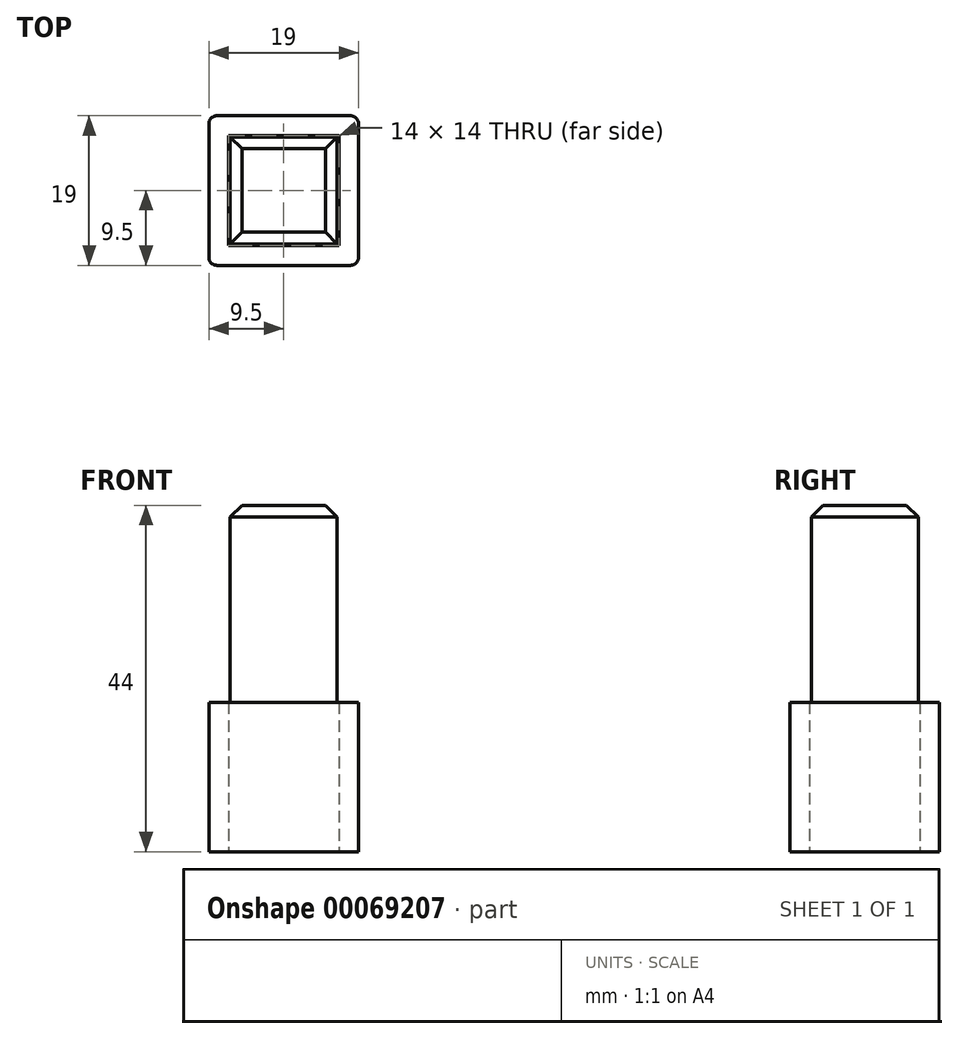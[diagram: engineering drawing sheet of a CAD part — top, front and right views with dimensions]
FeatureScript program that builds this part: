
annotation { "Feature Type Name" : "Feature", "Feature Type Description" : "" }
export const myFeature = defineFeature(function(context is Context, id is Id, definition is map)
    precondition{}
    {
        {
            var Q0;
            Q0=qCreatedBy(makeId("Top.planeOp"),FACE);
            var sketch = newSketch(context, id + "F0", { "sketchPlane" : qUnion([Q0])});
            skLineSegment(sketch, "E0.rect.bottom", {"start": v(9.5, 9.5) * mm, "end": v(-9.5, 9.5) * mm});
            skLineSegment(sketch, "E0.rect.top", {"start": v(9.5, -9.5) * mm, "end": v(-9.5, -9.5) * mm});
            skLineSegment(sketch, "E0.rect.left", {"start": v(9.5, 9.5) * mm, "end": v(9.5, -9.5) * mm});
            skLineSegment(sketch, "E0.rect.right", {"start": v(-9.5, 9.5) * mm, "end": v(-9.5, -9.5) * mm});
            skPoint(sketch, "E0.rect.middle", {"position": v(0, 0) * mm});
            skSolve(sketch);
        }
        {
            var Q0;
            Q0 = qSketchRegion(id + "F0", true);
            extrude(context, id + "F1", {"entities" : qUnion([Q0]), "depth" : (14 + 5) * mm});
        }
        {
            var Q0;
            Q0=makeQuery(id+"F1.opExtrude","CAP_FACE",FACE,{"disambiguationData":[OSD([sQuery(id+"F0.wireOp",EDGE,"E0.rect.bottom"),sQuery(id+"F0.wireOp",EDGE,"E0.rect.top"),sQuery(id+"F0.wireOp",EDGE,"E0.rect.left"),sQuery(id+"F0.wireOp",EDGE,"E0.rect.right")])],"isStart":false});
            shell(context, id + "F2", {"entities" : qUnion([Q0]), "thickness" : 2.5 * mm});
        }
        {
            var Q0;
            Q0=makeQuery(id+"F1.opExtrude","CAP_FACE",FACE,{"disambiguationData":[OSD([sQuery(id+"F0.wireOp",EDGE,"E0.rect.bottom"),sQuery(id+"F0.wireOp",EDGE,"E0.rect.top"),sQuery(id+"F0.wireOp",EDGE,"E0.rect.left"),sQuery(id+"F0.wireOp",EDGE,"E0.rect.right")])],"isStart":false});
            var sketch = newSketch(context, id + "F3", { "sketchPlane" : qUnion([Q0])});
            skLineSegment(sketch, "E1.rect.bottom", {"start": v(6.8, 6.8) * mm, "end": v(-6.8, 6.8) * mm});
            skLineSegment(sketch, "E1.rect.top", {"start": v(6.8, -6.8) * mm, "end": v(-6.8, -6.8) * mm});
            skLineSegment(sketch, "E1.rect.left", {"start": v(6.8, 6.8) * mm, "end": v(6.8, -6.8) * mm});
            skLineSegment(sketch, "E1.rect.right", {"start": v(-6.8, 6.8) * mm, "end": v(-6.8, -6.8) * mm});
            skPoint(sketch, "E1.rect.middle", {"position": v(0, 0) * mm});
            skSolve(sketch);
        }
        {
            var Q0;
            Q0 = qSketchRegion(id + "F3", true);
            extrude(context, id + "F4", {"entities" : qUnion([Q0]), "depth" : 25 * mm});
        }
        {
            var Q0;
            Q0=makeQuery(id+"F4.opExtrude","CAP_EDGE",EDGE,{"disambiguationData":[OSD([sQuery(id+"F3.wireOp",EDGE,"E1.rect.bottom")])],"isStart":false});
            var Q1;
            Q1=makeQuery(id+"F4.opExtrude","CAP_EDGE",EDGE,{"disambiguationData":[OSD([sQuery(id+"F3.wireOp",EDGE,"E1.rect.right")])],"isStart":false});
            var Q2;
            Q2=makeQuery(id+"F4.opExtrude","CAP_EDGE",EDGE,{"disambiguationData":[OSD([sQuery(id+"F3.wireOp",EDGE,"E1.rect.left")])],"isStart":false});
            var Q3;
            Q3=makeQuery(id+"F4.opExtrude","CAP_EDGE",EDGE,{"disambiguationData":[OSD([sQuery(id+"F3.wireOp",EDGE,"E1.rect.top")])],"isStart":false});
            chamfer(context, id + "F5", {"entities" : qUnion([Q0, Q1, Q2, Q3]), "width" : 1.5 * mm, "tangentPropagation" : true});
        }
        {
            var Q0;
            Q0=makeQuery(id+"F2.opShell","OFFSET_FACE",FACE,{"disambiguationData":[OSD([sQuery(id+"F0.wireOp",EDGE,"E0.rect.bottom"),sQuery(id+"F0.wireOp",EDGE,"E0.rect.top"),sQuery(id+"F0.wireOp",EDGE,"E0.rect.left"),sQuery(id+"F0.wireOp",EDGE,"E0.rect.right")])]});
            extrude(context, id + "F6", {"entities" : qUnion([Q0]), "operationType" : NewBodyOperationType.REMOVE, "oppositeDirection" : true, "depth" : 25 * mm});
        }
        {
            var Q0;
            Q0=makeQuery(id+"F1.opExtrude","SWEPT_EDGE",EDGE,{"disambiguationData":[OSD([sQuery(id+"F0.wireOp",EDGE,"E0.rect.bottom"),sQuery(id+"F0.wireOp",EDGE,"E0.rect.right")])]});
            var Q1;
            Q1=makeQuery(id+"F1.opExtrude","SWEPT_EDGE",EDGE,{"disambiguationData":[OSD([sQuery(id+"F0.wireOp",EDGE,"E0.rect.top"),sQuery(id+"F0.wireOp",EDGE,"E0.rect.right")])]});
            var Q2;
            Q2=makeQuery(id+"F1.opExtrude","SWEPT_EDGE",EDGE,{"disambiguationData":[OSD([sQuery(id+"F0.wireOp",EDGE,"E0.rect.top"),sQuery(id+"F0.wireOp",EDGE,"E0.rect.left")])]});
            var Q3;
            Q3=makeQuery(id+"F1.opExtrude","SWEPT_EDGE",EDGE,{"disambiguationData":[OSD([sQuery(id+"F0.wireOp",EDGE,"E0.rect.bottom"),sQuery(id+"F0.wireOp",EDGE,"E0.rect.left")])]});
            fillet(context, id + "F7", {"entities" : qUnion([Q0, Q1, Q2, Q3]), "radius" : 1 * mm, "tangentPropagation" : true, "allowEdgeOverflow" : false});
        }
    });
